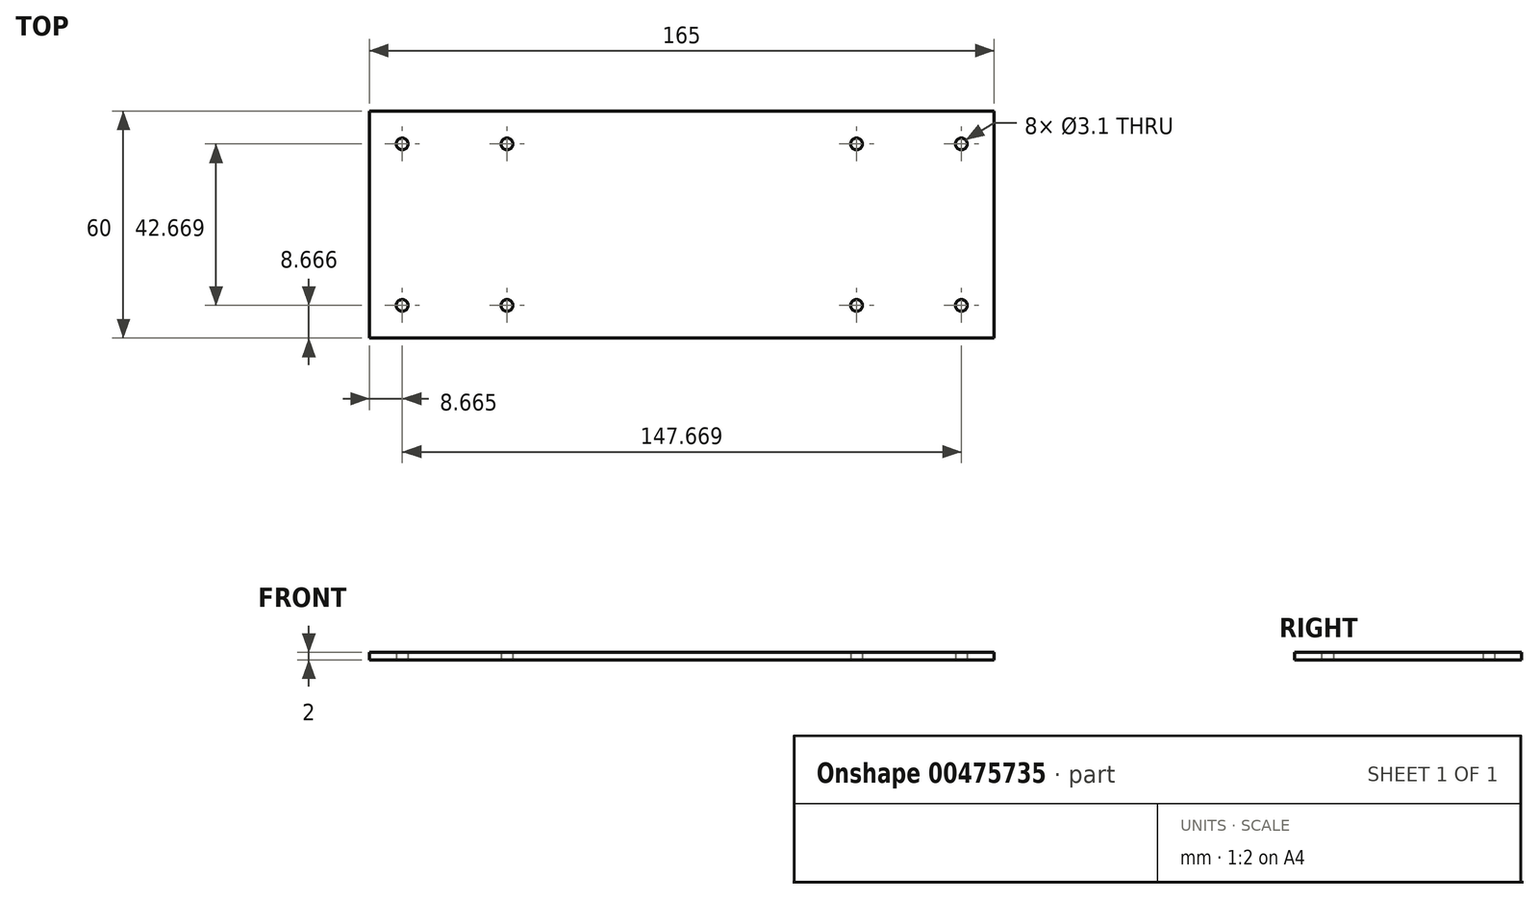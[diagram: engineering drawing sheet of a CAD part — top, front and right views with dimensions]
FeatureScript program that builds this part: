
annotation { "Feature Type Name" : "Feature", "Feature Type Description" : "" }
export const myFeature = defineFeature(function(context is Context, id is Id, definition is map)
    precondition{}
    {
        {
            var Q0;
            Q0=qCreatedBy(makeId("Top.planeOp"),FACE);
            var sketch = newSketch(context, id + "F0", { "sketchPlane" : qUnion([Q0])});
            skLineSegment(sketch, "E0.bottom", {"start": v(82.5, -30) * mm, "end": v(-82.5, -30) * mm});
            skLineSegment(sketch, "E0.top", {"start": v(82.5, 30) * mm, "end": v(-82.5, 30) * mm});
            skLineSegment(sketch, "E0.left", {"start": v(82.5, -30) * mm, "end": v(82.5, 30) * mm});
            skLineSegment(sketch, "E0.right", {"start": v(-82.5, -30) * mm, "end": v(-82.5, 30) * mm});
            skPoint(sketch, "E0.middle", {"position": v(0, 0) * mm});
            skCircle(sketch, "E1", {"center": v(-73.83, 21.33) * mm, "radius": 1.55 * mm});
            skCircle(sketch, "E2", {"center": v(73.83, 21.33) * mm, "radius": 1.55 * mm});
            skCircle(sketch, "E3", {"center": v(73.83, -21.33) * mm, "radius": 1.55 * mm});
            skCircle(sketch, "E4", {"center": v(-73.83, -21.33) * mm, "radius": 1.55 * mm});
            skLineSegment(sketch, "E5", {"start": v(73.83, -21.33) * mm, "end": v(73.83, -30) * mm, "construction": true});
            skLineSegment(sketch, "E6", {"start": v(73.83, 21.33) * mm, "end": v(73.83, 30) * mm, "construction": true});
            skLineSegment(sketch, "E7", {"start": v(73.83, -21.33) * mm, "end": v(82.5, -21.33) * mm, "construction": true});
            skLineSegment(sketch, "E8", {"start": v(-73.83, -21.33) * mm, "end": v(-46.17, -21.33) * mm, "construction": true});
            skLineSegment(sketch, "E9", {"start": v(73.83, -21.33) * mm, "end": v(46.17, -21.33) * mm, "construction": true});
            skLineSegment(sketch, "E10", {"start": v(73.83, 21.33) * mm, "end": v(46.17, 21.33) * mm, "construction": true});
            skLineSegment(sketch, "E11", {"start": v(-73.83, 21.33) * mm, "end": v(-46.17, 21.33) * mm, "construction": true});
            skCircle(sketch, "E12", {"center": v(-46.17, -21.33) * mm, "radius": 1.55 * mm});
            skCircle(sketch, "E13", {"center": v(-46.17, 21.33) * mm, "radius": 1.55 * mm});
            skCircle(sketch, "E14", {"center": v(46.17, 21.33) * mm, "radius": 1.55 * mm});
            skCircle(sketch, "E15", {"center": v(46.17, -21.33) * mm, "radius": 1.55 * mm});
            skSolve(sketch);
        }
        {
            var Q0;
            Q0=qSketchRegion(id+"F0",true);
            extrude(context, id + "F1", {"entities" : qUnion([Q0]), "depth" : 2 * mm});
        }
    });
